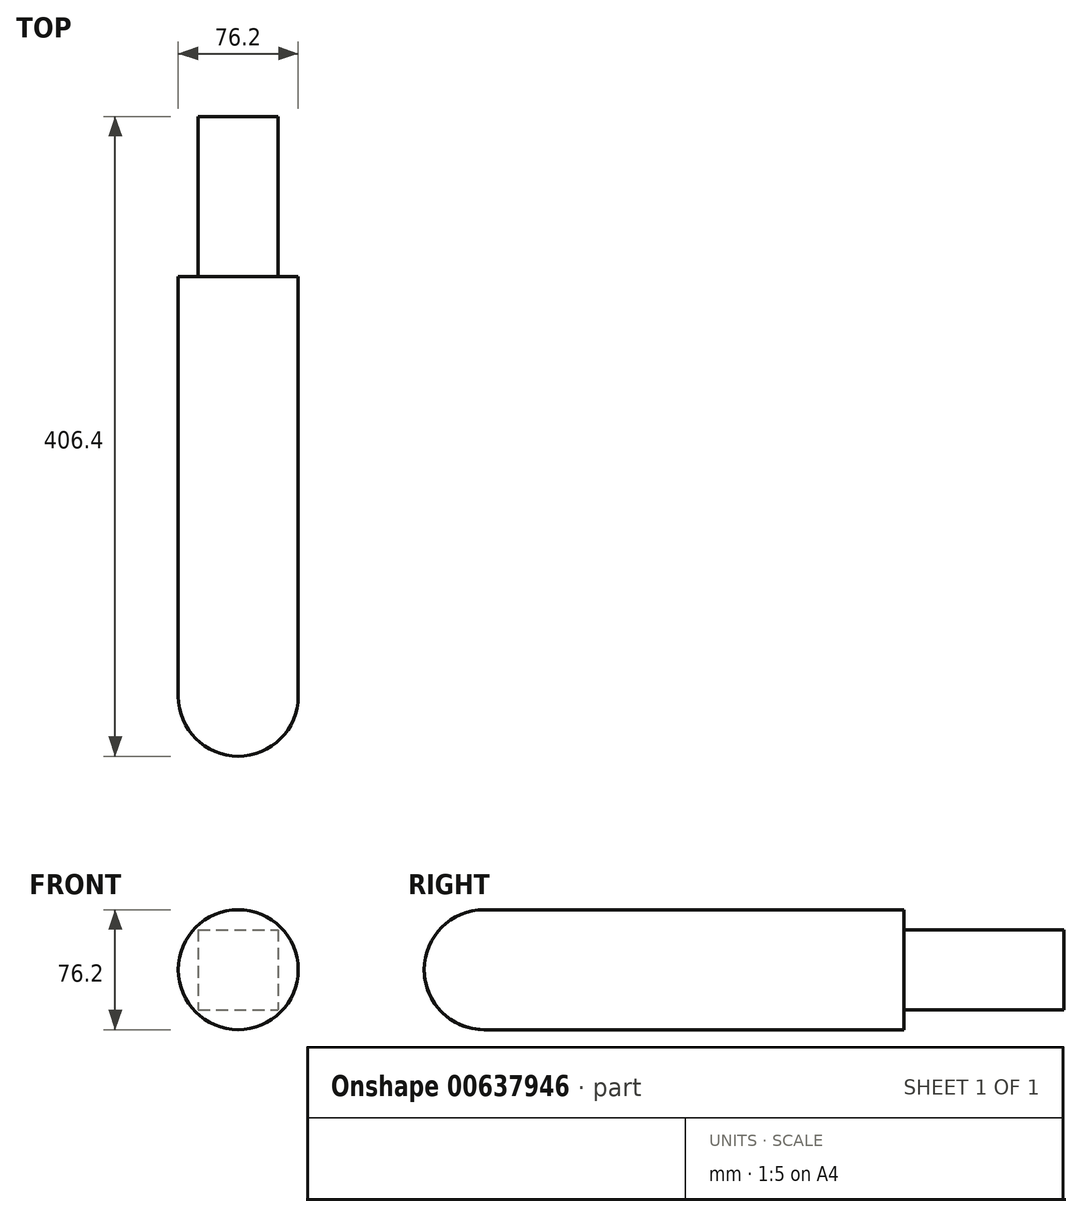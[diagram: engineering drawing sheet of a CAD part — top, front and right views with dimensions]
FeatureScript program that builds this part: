
annotation { "Feature Type Name" : "Feature", "Feature Type Description" : "" }
export const myFeature = defineFeature(function(context is Context, id is Id, definition is map)
    precondition{}
    {
        {
            var Q0;
            Q0=qCreatedBy(makeId("Front.planeOp"),FACE);
            var sketch = newSketch(context, id + "F0", { "sketchPlane" : qUnion([Q0])});
            skLineSegment(sketch, "E0.bottom", {"start": v(-25.4, 25.4) * mm, "end": v(25.4, 25.4) * mm});
            skLineSegment(sketch, "E0.top", {"start": v(-25.4, -25.4) * mm, "end": v(25.4, -25.4) * mm});
            skLineSegment(sketch, "E0.left", {"start": v(-25.4, 25.4) * mm, "end": v(-25.4, -25.4) * mm});
            skLineSegment(sketch, "E0.right", {"start": v(25.4, 25.4) * mm, "end": v(25.4, -25.4) * mm});
            skPoint(sketch, "E0.middle", {"position": v(0, 0) * mm});
            skSolve(sketch);
        }
        {
            var Q0;
            Q0=makeQuery(id+"F0.imprint","IMPRINT",FACE,{"disambiguationData":[TD([[makeQuery(id+"F0.imprint","IMPRINT",EDGE,{"derivedFrom":sQuery(id+"F0.wireOp",EDGE,"E0.bottom")}),-1.0]])]});
            extrude(context, id + "F1", {"entities" : qUnion([Q0]), "depth" : 101.6 * mm, "offsetDistance" : 25.4 * mm});
        }
        {
            var Q0;
            Q0=makeQuery(id+"F1.opExtrude","CAP_FACE",FACE,{"disambiguationData":[OSD([sQuery(id+"F0.wireOp",EDGE,"E0.bottom"),sQuery(id+"F0.wireOp",EDGE,"E0.top"),sQuery(id+"F0.wireOp",EDGE,"E0.left"),sQuery(id+"F0.wireOp",EDGE,"E0.right")])],"isStart":false});
            var sketch = newSketch(context, id + "F2", { "sketchPlane" : qUnion([Q0])});
            skCircle(sketch, "E1", {"center": v(0, 0) * mm, "radius": 38.1 * mm});
            skSolve(sketch);
        }
        {
            var Q0;
            Q0=makeQuery(id+"F2.imprint","IMPRINT",FACE,{"disambiguationData":[TD([[makeQuery(id+"F2.imprint","IMPRINT",EDGE,{"derivedFrom":sQuery(id+"F2.wireOp",EDGE,"E1")}),1.0]])]});
            var Q1;
            Q1=makeQuery(id+"F2.imprint","IMPRINT",FACE,{"disambiguationData":[TD([[makeQuery(id+"F2.imprint","IMPRINT",EDGE,{"derivedFrom":makeQuery(id+"F1.opExtrude","CAP_EDGE",EDGE,{"disambiguationData":[OSD([sQuery(id+"F0.wireOp",EDGE,"E0.bottom")])],"isStart":false})}),-1.0]])]});
            extrude(context, id + "F3", {"entities" : qUnion([Q0, Q1]), "operationType" : NewBodyOperationType.ADD, "depth" : 304.8 * mm, "offsetDistance" : 25.4 * mm});
        }
        {
            var Q0;
            Q0=makeQuery(id+"F3.opExtrude","CAP_FACE",FACE,{"disambiguationData":[OSD([sQuery(id+"F2.wireOp",EDGE,"E1")])],"isStart":false});
            fillet(context, id + "F4", {"entities" : qUnion([Q0]), "radius" : 38.1 * mm, "tangentPropagation" : true, "allowEdgeOverflow" : false});
        }
    });
